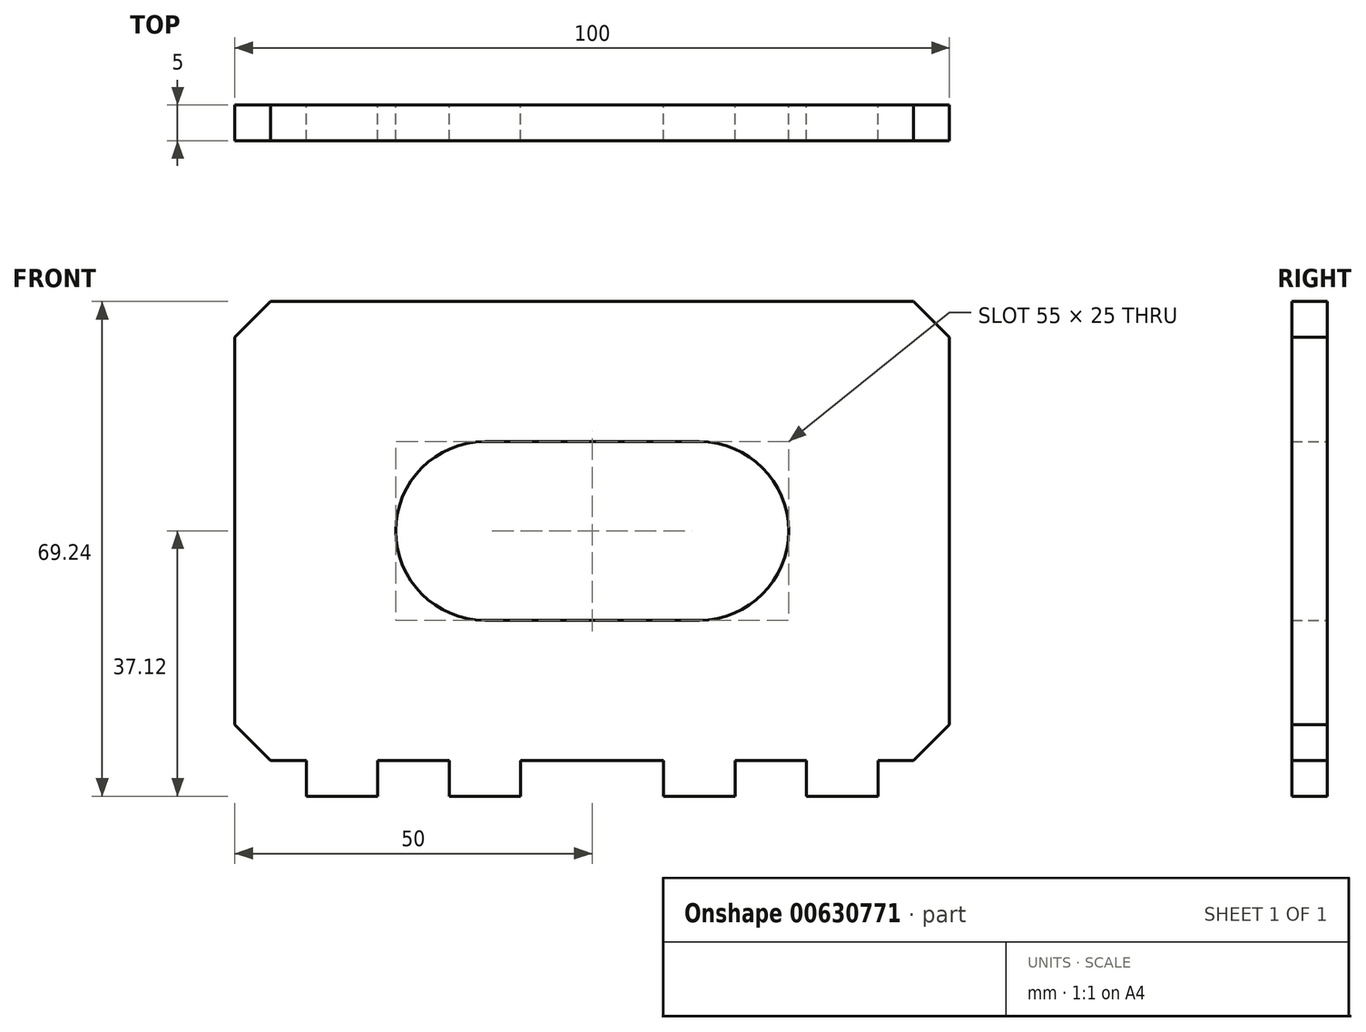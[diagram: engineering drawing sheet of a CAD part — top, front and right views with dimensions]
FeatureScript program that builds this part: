
annotation { "Feature Type Name" : "Feature", "Feature Type Description" : "" }
export const myFeature = defineFeature(function(context is Context, id is Id, definition is map)
    precondition{}
    {
        {
            var Q0;
            Q0=qCreatedBy(makeId("Front.planeOp"),FACE);
            var sketch = newSketch(context, id + "F0", { "sketchPlane" : qUnion([Q0])});
            skLineSegment(sketch, "E0.bottom", {"start": v(-50, 32.12) * mm, "end": v(50, 32.12) * mm});
            skLineSegment(sketch, "E0.top", {"start": v(-50, -32.13) * mm, "end": v(50, -32.13) * mm});
            skLineSegment(sketch, "E0.left", {"start": v(-50, 32.12) * mm, "end": v(-50, -32.13) * mm});
            skLineSegment(sketch, "E0.right", {"start": v(50, 32.12) * mm, "end": v(50, -32.13) * mm});
            skLineSegment(sketch, "E1", {"start": v(-15, 0) * mm, "end": v(15, 0) * mm});
            skArc(sketch, "E2.0.startCap", {"start": v(-15, -12.5) * mm, "mid": v(-27.5, 0) * mm, "end": v(-15, 12.5) * mm});
            skArc(sketch, "E2.0.endCap", {"start": v(15, 12.5) * mm, "mid": v(27.5, 0) * mm, "end": v(15, -12.5) * mm});
            skLineSegment(sketch, "E2.0.left", {"start": v(-15, 12.5) * mm, "end": v(15, 12.5) * mm});
            skLineSegment(sketch, "E2.0.right", {"start": v(-15, -12.5) * mm, "end": v(15, -12.5) * mm});
            skSolve(sketch);
        }
        {
            var Q0;
            Q0=makeQuery(id+"F0.imprint","IMPRINT",FACE,{"disambiguationData":[TD([[makeQuery(id+"F0.imprint","IMPRINT",EDGE,{"derivedFrom":sQuery(id+"F0.wireOp",EDGE,"E0.bottom")}),-1.0]])]});
            extrude(context, id + "F1", {"entities" : qUnion([Q0]), "depth" : 5 * mm, "offsetDistance" : 25 * mm});
        }
        {
            var Q0;
            Q0=makeQuery(id+"F1.opExtrude","SWEPT_EDGE",EDGE,{"disambiguationData":[OSD([sQuery(id+"F0.wireOp",EDGE,"E0.bottom"),sQuery(id+"F0.wireOp",EDGE,"E0.left")])]});
            var Q1;
            Q1=makeQuery(id+"F1.opExtrude","SWEPT_EDGE",EDGE,{"disambiguationData":[OSD([sQuery(id+"F0.wireOp",EDGE,"E0.bottom"),sQuery(id+"F0.wireOp",EDGE,"E0.right")])]});
            var Q2;
            Q2=makeQuery(id+"F1.opExtrude","SWEPT_EDGE",EDGE,{"disambiguationData":[OSD([sQuery(id+"F0.wireOp",EDGE,"E0.top"),sQuery(id+"F0.wireOp",EDGE,"E0.left")])]});
            var Q3;
            Q3=makeQuery(id+"F1.opExtrude","SWEPT_EDGE",EDGE,{"disambiguationData":[OSD([sQuery(id+"F0.wireOp",EDGE,"E0.top"),sQuery(id+"F0.wireOp",EDGE,"E0.right")])]});
            chamfer(context, id + "F2", {"entities" : qUnion([Q0, Q1, Q2, Q3]), "width" : 5 * mm, "tangentPropagation" : true});
        }
        {
            var Q0;
            Q0=makeQuery(id+"F1.opExtrude","SWEPT_FACE",FACE,{"disambiguationData":[OSD([sQuery(id+"F0.wireOp",EDGE,"E0.top")])]});
            var sketch = newSketch(context, id + "F3", { "sketchPlane" : qUnion([Q0])});
            skLineSegment(sketch, "E3.bottom", {"start": v(-40, 5) * mm, "end": v(-30, 5) * mm});
            skLineSegment(sketch, "E3.top", {"start": v(-40, 0) * mm, "end": v(-30, 0) * mm});
            skLineSegment(sketch, "E3.left", {"start": v(-40, 5) * mm, "end": v(-40, 0) * mm});
            skLineSegment(sketch, "E3.right", {"start": v(-30, 5) * mm, "end": v(-30, 0) * mm});
            skLineSegment(sketch, "E4.bottom", {"start": v(-20, 5) * mm, "end": v(-10, 5) * mm});
            skLineSegment(sketch, "E4.top", {"start": v(-20, 0) * mm, "end": v(-10, 0) * mm});
            skLineSegment(sketch, "E4.left", {"start": v(-20, 5) * mm, "end": v(-20, 0) * mm});
            skLineSegment(sketch, "E4.right", {"start": v(-10, 5) * mm, "end": v(-10, 0) * mm});
            skLineSegment(sketch, "E5.bottom", {"start": v(10, 5) * mm, "end": v(20, 5) * mm});
            skLineSegment(sketch, "E5.top", {"start": v(10, 0) * mm, "end": v(20, 0) * mm});
            skLineSegment(sketch, "E5.left", {"start": v(10, 5) * mm, "end": v(10, 0) * mm});
            skLineSegment(sketch, "E5.right", {"start": v(20, 5) * mm, "end": v(20, 0) * mm});
            skLineSegment(sketch, "E6.bottom", {"start": v(30, 5) * mm, "end": v(40, 5) * mm});
            skLineSegment(sketch, "E6.top", {"start": v(30, 0) * mm, "end": v(40, 0) * mm});
            skLineSegment(sketch, "E6.left", {"start": v(30, 5) * mm, "end": v(30, 0) * mm});
            skLineSegment(sketch, "E6.right", {"start": v(40, 5) * mm, "end": v(40, 0) * mm});
            skLineSegment(sketch, "E7", {"start": v(-25, 9.91) * mm, "end": v(-25, -12.22) * mm, "construction": true});
            skLineSegment(sketch, "E8", {"start": v(25, 10.76) * mm, "end": v(25, -11.94) * mm, "construction": true});
            skSolve(sketch);
        }
        {
            var Q0;
            Q0=makeQuery(id+"F3.imprint","IMPRINT",FACE,{"disambiguationData":[TD([[makeQuery(id+"F3.imprint","IMPRINT",EDGE,{"derivedFrom":sQuery(id+"F3.wireOp",EDGE,"E6.bottom")}),-1.0]])]});
            var Q1;
            Q1=makeQuery(id+"F3.imprint","IMPRINT",FACE,{"disambiguationData":[TD([[makeQuery(id+"F3.imprint","IMPRINT",EDGE,{"derivedFrom":sQuery(id+"F3.wireOp",EDGE,"E5.bottom")}),-1.0]])]});
            var Q2;
            Q2=makeQuery(id+"F3.imprint","IMPRINT",FACE,{"disambiguationData":[TD([[makeQuery(id+"F3.imprint","IMPRINT",EDGE,{"derivedFrom":sQuery(id+"F3.wireOp",EDGE,"E4.bottom")}),-1.0]])]});
            var Q3;
            Q3=makeQuery(id+"F3.imprint","IMPRINT",FACE,{"disambiguationData":[TD([[makeQuery(id+"F3.imprint","IMPRINT",EDGE,{"derivedFrom":sQuery(id+"F3.wireOp",EDGE,"E3.bottom")}),-1.0]])]});
            extrude(context, id + "F4", {"entities" : qUnion([Q0, Q1, Q2, Q3]), "operationType" : NewBodyOperationType.ADD, "depth" : 5 * mm, "offsetDistance" : 25 * mm});
        }
    });
